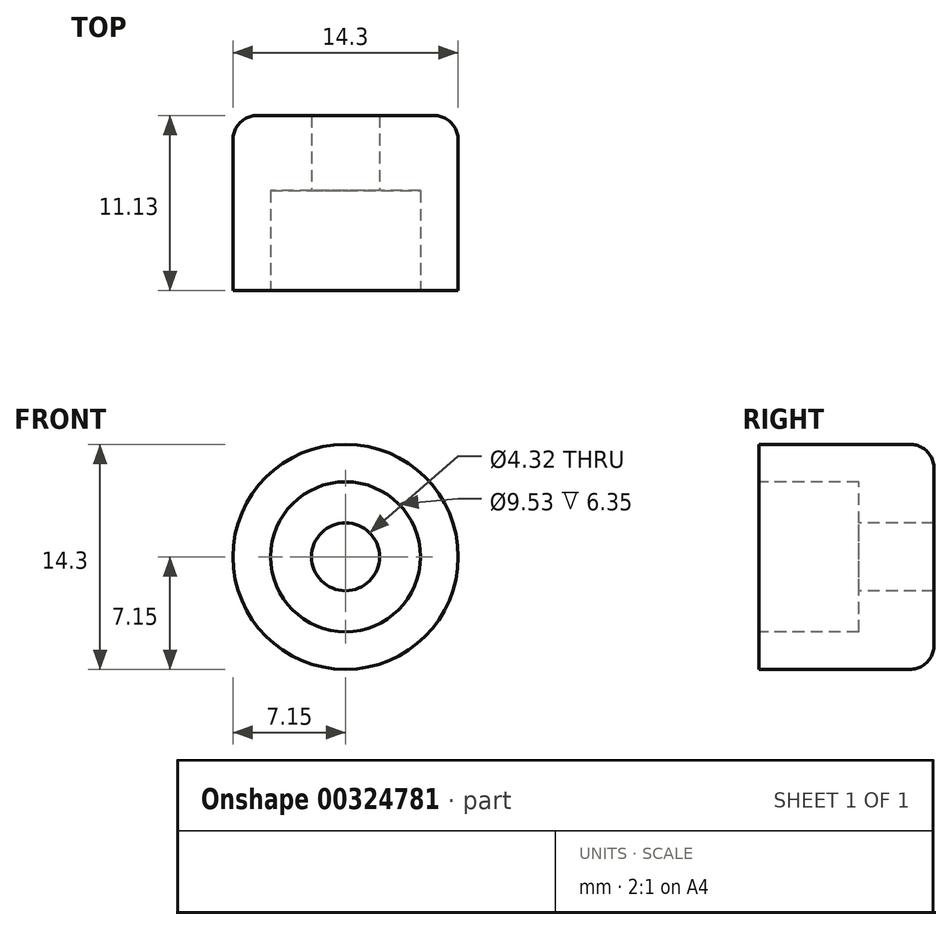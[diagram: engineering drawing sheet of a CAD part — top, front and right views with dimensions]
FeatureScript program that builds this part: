
annotation { "Feature Type Name" : "Feature", "Feature Type Description" : "" }
export const myFeature = defineFeature(function(context is Context, id is Id, definition is map)
    precondition{}
    {
        {
            var Q0;
            Q0=qCreatedBy(makeId("Front.planeOp"),FACE);
            var sketch = newSketch(context, id + "F0", { "sketchPlane" : qUnion([Q0])});
            skCircle(sketch, "E0", {"center": v(0, 0) * mm, "radius": 7.15 * mm});
            skSolve(sketch);
        }
        {
            var Q0;
            Q0=makeQuery(id+"F0.imprint","IMPRINT",FACE,{"disambiguationData":[TD([[makeQuery(id+"F0.imprint","IMPRINT",EDGE,{"derivedFrom":sQuery(id+"F0.wireOp",EDGE,"E0")}),1.0]])]});
            extrude(context, id + "F1", {"entities" : qUnion([Q0]), "depth" : 11.13 * mm, "offsetDistance" : 25.4 * mm});
        }
        {
            var Q0;
            Q0=makeQuery(id+"F1.opExtrude","CAP_FACE",FACE,{"disambiguationData":[OSD([sQuery(id+"F0.wireOp",EDGE,"E0")])],"isStart":false});
            var sketch = newSketch(context, id + "F2", { "sketchPlane" : qUnion([Q0])});
            skCircle(sketch, "E1", {"center": v(0, 0) * mm, "radius": 2.16 * mm});
            skSolve(sketch);
        }
        {
            var Q0;
            Q0=makeQuery(id+"F2.imprint","IMPRINT",FACE,{"disambiguationData":[TD([[makeQuery(id+"F2.imprint","IMPRINT",EDGE,{"derivedFrom":sQuery(id+"F2.wireOp",EDGE,"E1")}),1.0]])]});
            extrude(context, id + "F3", {"entities" : qUnion([Q0]), "operationType" : NewBodyOperationType.REMOVE, "endBound" : BoundingType.THROUGH_ALL, "oppositeDirection" : true, "depth" : 25.4 * mm, "offsetDistance" : 25.4 * mm});
        }
        {
            var Q0;
            Q0=makeQuery(id+"F1.opExtrude","CAP_FACE",FACE,{"disambiguationData":[OSD([sQuery(id+"F0.wireOp",EDGE,"E0")])],"isStart":false});
            var sketch = newSketch(context, id + "F4", { "sketchPlane" : qUnion([Q0])});
            skCircle(sketch, "E2", {"center": v(0, 0) * mm, "radius": 4.76 * mm});
            skSolve(sketch);
        }
        {
            var Q0;
            Q0=makeQuery(id+"F4.imprint","IMPRINT",FACE,{"disambiguationData":[TD([[makeQuery(id+"F4.imprint","IMPRINT",EDGE,{"derivedFrom":sQuery(id+"F4.wireOp",EDGE,"E2")}),1.0]])]});
            extrude(context, id + "F5", {"entities" : qUnion([Q0]), "operationType" : NewBodyOperationType.REMOVE, "oppositeDirection" : true, "depth" : 6.35 * mm, "offsetDistance" : 25.4 * mm});
        }
        {
            var Q0;
            Q0=makeQuery(id+"F1.opExtrude","CAP_EDGE",EDGE,{"disambiguationData":[OSD([sQuery(id+"F0.wireOp",EDGE,"E0")])],"isStart":true});
            fillet(context, id + "F6", {"entities" : qUnion([Q0]), "radius" : 1.52 * mm, "tangentPropagation" : true, "allowEdgeOverflow" : false});
        }
    });
